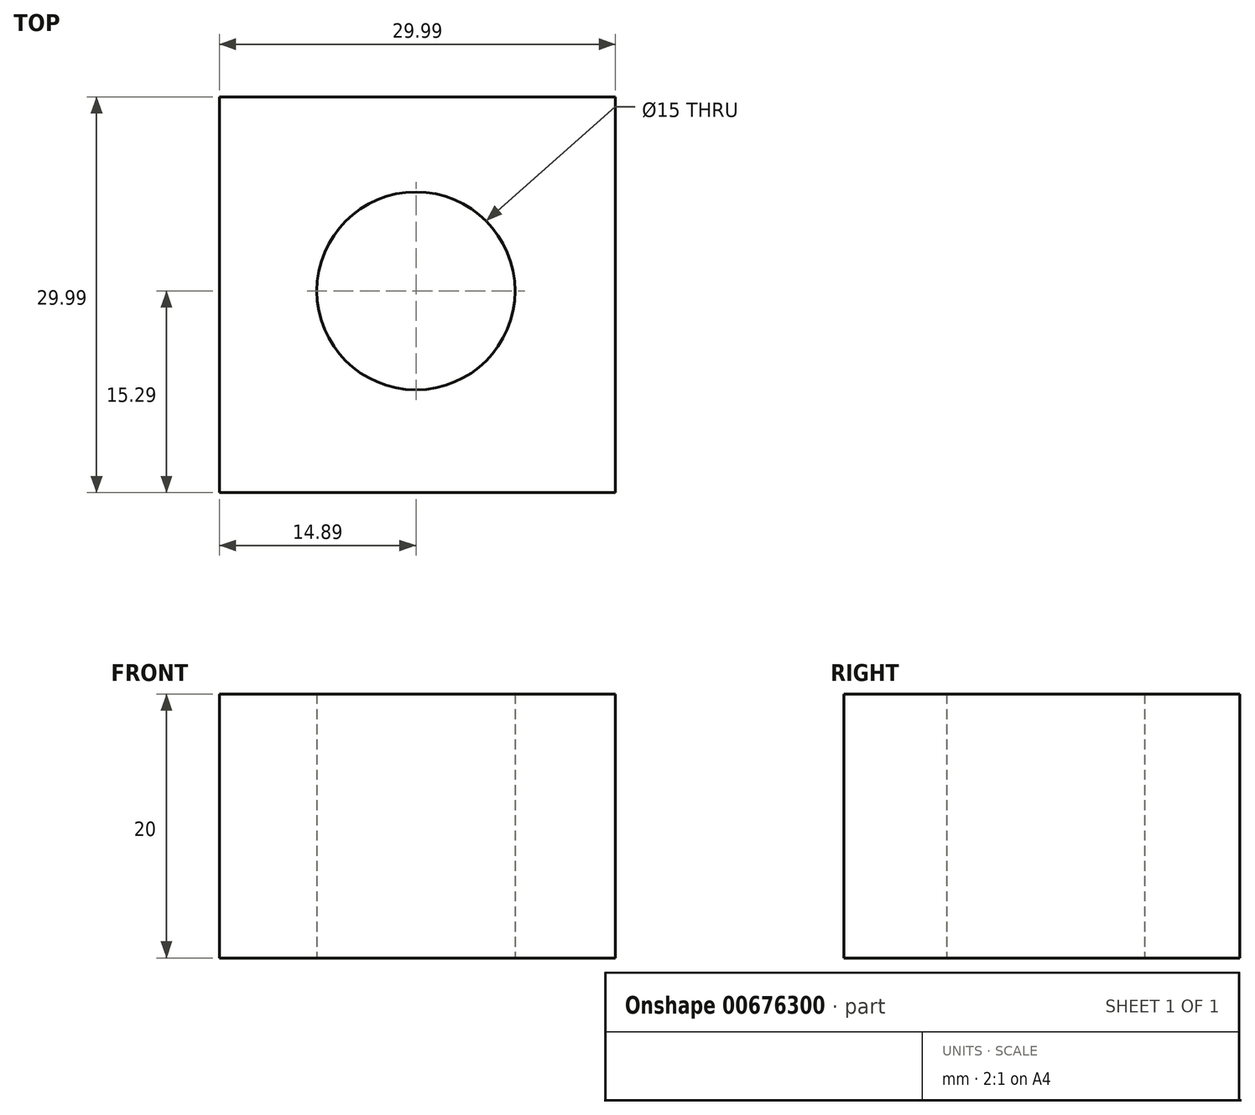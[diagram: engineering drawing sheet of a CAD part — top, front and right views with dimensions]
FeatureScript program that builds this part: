
annotation { "Feature Type Name" : "Feature", "Feature Type Description" : "" }
export const myFeature = defineFeature(function(context is Context, id is Id, definition is map)
    precondition{}
    {
        {
            var Q0;
            Q0=qCreatedBy(makeId("Top.planeOp"),FACE);
            var sketch = newSketch(context, id + "F0", { "sketchPlane" : qUnion([Q0])});
            skLineSegment(sketch, "E0.bottom", {"start": v(-14.89, 14.7) * mm, "end": v(15.1, 14.7) * mm});
            skLineSegment(sketch, "E0.top", {"start": v(-14.89, -15.29) * mm, "end": v(15.1, -15.29) * mm});
            skLineSegment(sketch, "E0.left", {"start": v(-14.89, 14.7) * mm, "end": v(-14.89, -15.29) * mm});
            skLineSegment(sketch, "E0.right", {"start": v(15.1, 14.7) * mm, "end": v(15.1, -15.29) * mm});
            skCircle(sketch, "E1", {"center": v(0, 0) * mm, "radius": 7.5 * mm});
            skSolve(sketch);
        }
        {
            var Q0;
            Q0=makeQuery(id+"F0.imprint","IMPRINT",FACE,{"disambiguationData":[TD([[makeQuery(id+"F0.imprint","IMPRINT",EDGE,{"derivedFrom":sQuery(id+"F0.wireOp",EDGE,"E0.bottom")}),-1.0]])]});
            extrude(context, id + "F1", {"entities" : qUnion([Q0]), "depth" : 20 * mm, "offsetDistance" : 25.4 * mm});
        }
    });
